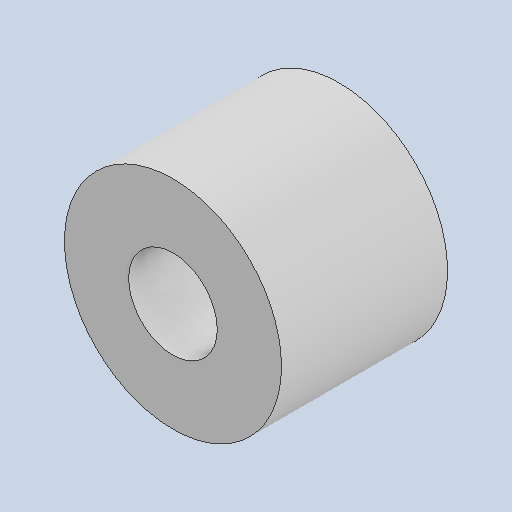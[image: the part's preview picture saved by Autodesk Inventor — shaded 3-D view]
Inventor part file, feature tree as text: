
AUTODESK INVENTOR PART (.ipt)
format: ipt  version: 2024 (Build 280153000, 153)  size: 94,720 bytes
history: native  units: in
note: dims shown in document units (in); Inventor stores cm internally (conversion verified against a paired STEP export)
features: other x3, sketch x1
ambient origin geometry x8: Origin, YZ Plane, XZ Plane, XY Plane, X Axis, Y Axis, Z Axis, Center Point
bodies: Solid1 (feature_tree)
feature tree (4):
  other  "Part3.ipt"
  other  "Solid1::Part3.ipt"
  other  "TaggingFeature1"
  sketch  "Sketch1"  dims[d0=0.3937in]
